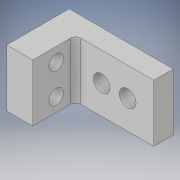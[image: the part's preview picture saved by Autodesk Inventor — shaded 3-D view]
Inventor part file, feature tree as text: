
AUTODESK INVENTOR PART (.ipt)
format: ipt  version: 2017 (Build 210142000, 142)  size: 135,168 bytes
history: native  units: in
note: dims shown in document units (in); Inventor stores cm internally (conversion verified against a paired STEP export)
features: sketch x4, extrude x2, hole x2, fillet x1
ambient origin geometry x8: Origin, YZ Plane, XZ Plane, XY Plane, X Axis, Y Axis, Z Axis, Center Point
bodies: Solid1 (feature_tree)
feature tree (9):
  extrude  "Extrusion1"  Depth=0.6in
  extrude  "Extrusion2"  Depth=0.1875in
  hole  "Hole1"  [1 undecoded]
  fillet  "Fillet1"  Radius=0.25in
  hole  "Hole2"  [1 undecoded]
  sketch  "Sketch1"  dims[d0=0.55in d1=0.6in]
  sketch  "Sketch2"  dims[d2=0.25in d3=0.0in d4=0.1875in]
  sketch  "Sketch3"  dims[d5=0.75in d6=0.0in]
  sketch  "Sketch4"  dims[d10=0.14in d11=0.75in d12=0.375in d13=0.25in d14=0.5635in d15=1.0in d16=0.8108in d17=0.05in d19=0.25in d20=0.25in d21=0.16in d22=0.75in d23=0.375in d24=0.25in d25=0.5635in d26=1.0in d27=0.8108in d28=0.375in d29=0.375in d30=0.287in d31=0.1315in d32=0.55in]
note: 2 required parameter values undecoded (feature->parameter linkage not recoverable at this tier; creation-order binding heuristic only, values carry confidence <= 0.55)
